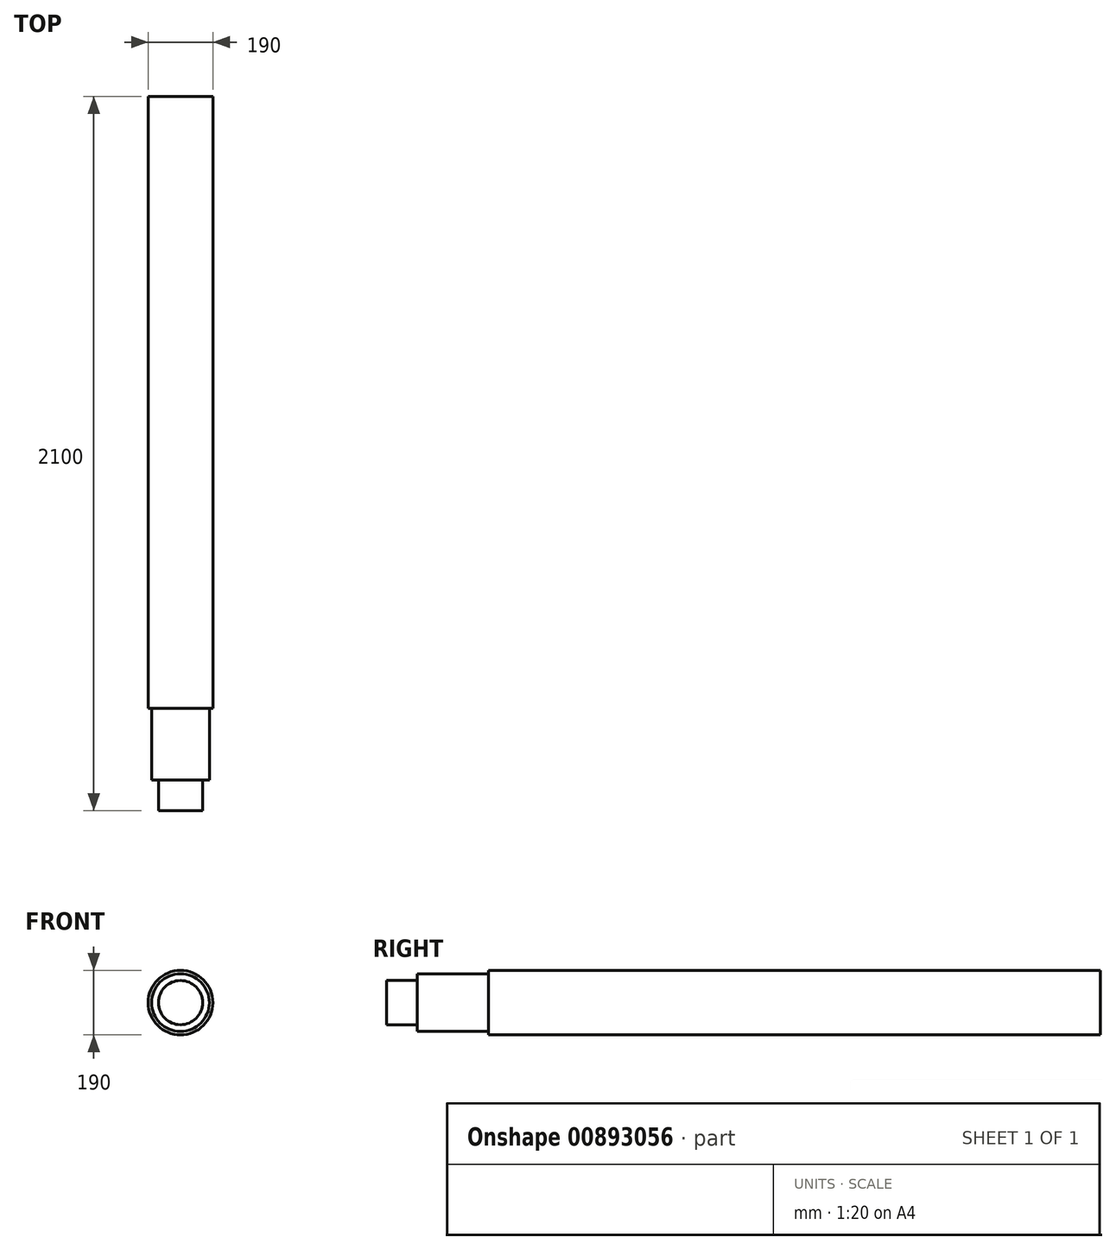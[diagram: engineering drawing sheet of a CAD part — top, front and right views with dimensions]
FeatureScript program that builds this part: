
annotation { "Feature Type Name" : "Feature", "Feature Type Description" : "" }
export const myFeature = defineFeature(function(context is Context, id is Id, definition is map)
    precondition{}
    {
        {
            var Q0;
            Q0=qCreatedBy(makeId("Front.planeOp"),FACE);
            var sketch = newSketch(context, id + "F0", { "sketchPlane" : qUnion([Q0])});
            skCircle(sketch, "E0", {"center": v(0, 0) * mm, "radius": 95 * mm});
            skSolve(sketch);
        }
        {
            var Q0;
            Q0 = qSketchRegion(id + "F0", true);
            extrude(context, id + "F1", {"entities" : qUnion([Q0]), "depth" : 2100 * mm, "offsetDistance" : 25 * mm});
        }
        {
            var Q0;
            Q0=makeQuery(id+"F1.opExtrude","CAP_FACE",FACE,{"disambiguationData":[OSD([sQuery(id+"F0.wireOp",EDGE,"E0")])],"isStart":false});
            var sketch = newSketch(context, id + "F2", { "sketchPlane" : qUnion([Q0])});
            skCircle(sketch, "E1", {"center": v(0, 0) * mm, "radius": 84.88 * mm});
            skCircle(sketch, "E2", {"center": v(0, 0) * mm, "radius": 144.61 * mm});
            skSolve(sketch);
        }
        {
            var Q0;
            Q0 = qSketchRegion(id + "F2", true);
            extrude(context, id + "F3", {"entities" : qUnion([Q0]), "operationType" : NewBodyOperationType.REMOVE, "oppositeDirection" : true, "depth" : 300 * mm, "offsetDistance" : 25 * mm});
        }
        {
            var Q0;
            Q0=makeQuery(id+"F1.opExtrude","CAP_FACE",FACE,{"disambiguationData":[OSD([sQuery(id+"F0.wireOp",EDGE,"E0")])],"isStart":false});
            var sketch = newSketch(context, id + "F4", { "sketchPlane" : qUnion([Q0])});
            skCircle(sketch, "E3", {"center": v(0, 0) * mm, "radius": 64.95 * mm});
            skCircle(sketch, "E4", {"center": v(0, 0) * mm, "radius": 133 * mm});
            skSolve(sketch);
        }
        {
            var Q0;
            Q0 = qSketchRegion(id + "F4", true);
            extrude(context, id + "F5", {"entities" : qUnion([Q0]), "operationType" : NewBodyOperationType.REMOVE, "oppositeDirection" : true, "depth" : 90 * mm, "offsetDistance" : 25 * mm});
        }
    });
